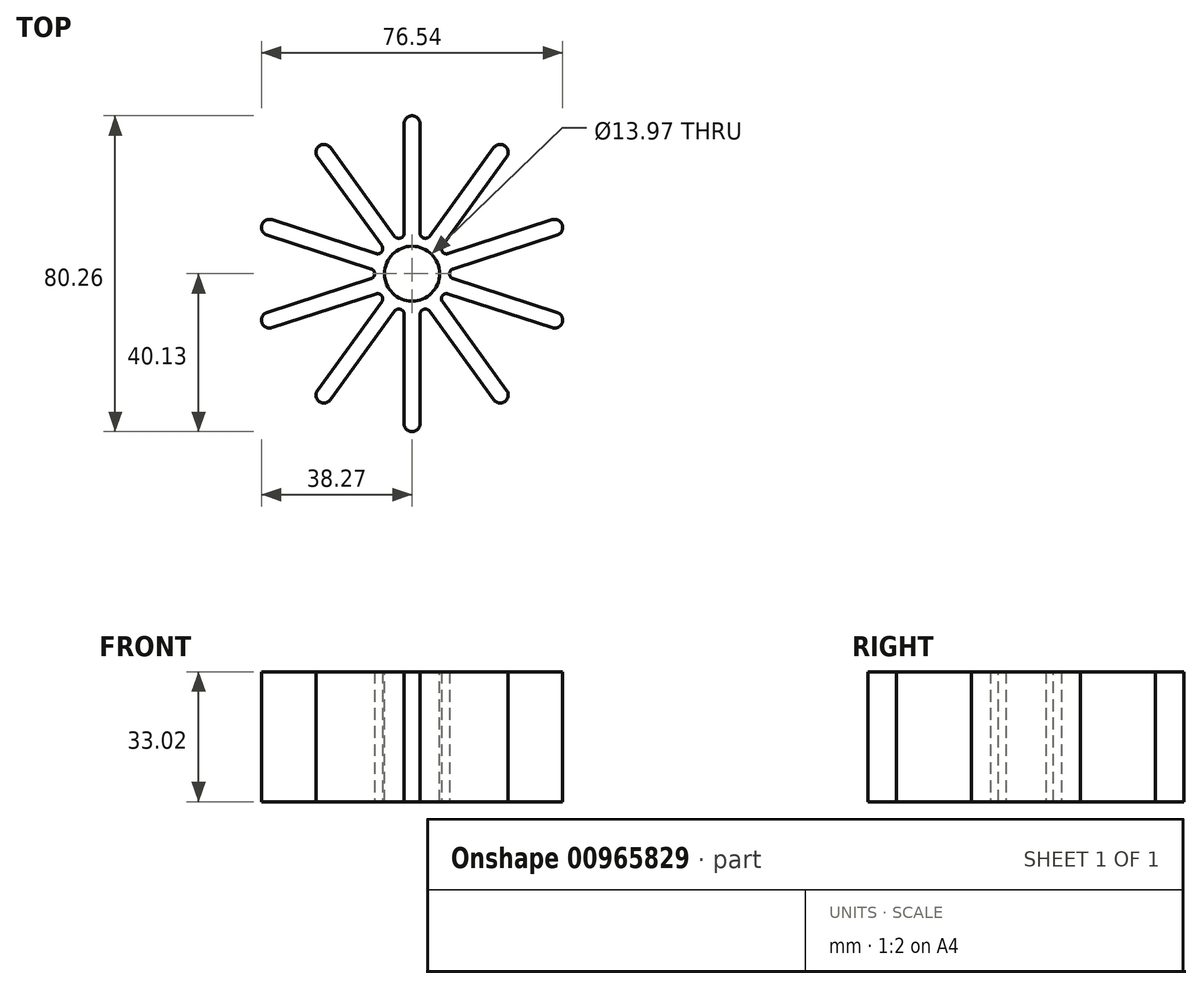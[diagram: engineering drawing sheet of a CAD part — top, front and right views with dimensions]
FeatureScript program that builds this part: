
annotation { "Feature Type Name" : "Feature", "Feature Type Description" : "" }
export const myFeature = defineFeature(function(context is Context, id is Id, definition is map)
    precondition{}
    {
        {
            var Q0;
            Q0=qCreatedBy(makeId("Top.planeOp"),FACE);
            var sketch = newSketch(context, id + "F0", { "sketchPlane" : qUnion([Q0])});
            skLineSegment(sketch, "E0", {"start": v(0, 0) * mm, "end": v(-2.03, 0) * mm});
            skLineSegment(sketch, "E1", {"start": v(-2.03, 0) * mm, "end": v(-2.03, 38.1) * mm});
            skArc(sketch, "E2", {"start": v(-2.03, 38.1) * mm, "mid": v(-1.44, 39.54) * mm, "end": v(0, 40.13) * mm});
            skLineSegment(sketch, "E3", {"start": v(0, 40.13) * mm, "end": v(0, 0) * mm});
            skArc(sketch, "E4.MirrorCS", {"start": v(2.03, 38.1) * mm, "mid": v(1.44, 39.54) * mm, "end": v(0, 40.13) * mm});
            skLineSegment(sketch, "E5.MirrorCS", {"start": v(2.03, 0) * mm, "end": v(2.03, 38.1) * mm});
            skLineSegment(sketch, "E6.MirrorCS", {"start": v(0, 0) * mm, "end": v(2.03, 0) * mm});
            skLineSegment(sketch, "E7.1.0", {"start": v(1.64, 1.2) * mm, "end": v(-20.75, 32.02) * mm});
            skLineSegment(sketch, "E7.1.1", {"start": v(-1.64, -1.2) * mm, "end": v(-24.04, 29.63) * mm});
            skLineSegment(sketch, "E7.1.2", {"start": v(-23.59, 32.47) * mm, "end": v(0, 0) * mm});
            skArc(sketch, "E7.1.3", {"start": v(-20.75, 32.02) * mm, "mid": v(-22.08, 32.83) * mm, "end": v(-23.59, 32.47) * mm});
            skArc(sketch, "E7.1.4", {"start": v(-24.04, 29.63) * mm, "mid": v(-24.4, 31.14) * mm, "end": v(-23.59, 32.47) * mm});
            skLineSegment(sketch, "E7.1.5", {"start": v(0, 0) * mm, "end": v(1.64, 1.2) * mm});
            skLineSegment(sketch, "E7.1.6", {"start": v(0, 0) * mm, "end": v(-1.64, -1.2) * mm});
            skLineSegment(sketch, "E7.2.0", {"start": v(0.63, 1.93) * mm, "end": v(-35.6, 13.7) * mm});
            skLineSegment(sketch, "E7.2.1", {"start": v(-0.63, -1.93) * mm, "end": v(-36.86, 9.84) * mm});
            skLineSegment(sketch, "E7.2.2", {"start": v(-38.17, 12.4) * mm, "end": v(0, 0) * mm});
            skArc(sketch, "E7.2.3", {"start": v(-35.6, 13.7) * mm, "mid": v(-37.16, 13.58) * mm, "end": v(-38.17, 12.4) * mm});
            skArc(sketch, "E7.2.4", {"start": v(-36.86, 9.84) * mm, "mid": v(-38.05, 10.85) * mm, "end": v(-38.17, 12.4) * mm});
            skLineSegment(sketch, "E7.2.5", {"start": v(0, 0) * mm, "end": v(0.63, 1.93) * mm});
            skLineSegment(sketch, "E7.2.6", {"start": v(0, 0) * mm, "end": v(-0.63, -1.93) * mm});
            skLineSegment(sketch, "E7.3.0", {"start": v(-0.63, 1.93) * mm, "end": v(-36.86, -9.84) * mm});
            skLineSegment(sketch, "E7.3.1", {"start": v(0.63, -1.93) * mm, "end": v(-35.6, -13.7) * mm});
            skLineSegment(sketch, "E7.3.2", {"start": v(-38.17, -12.4) * mm, "end": v(0, 0) * mm});
            skArc(sketch, "E7.3.3", {"start": v(-36.86, -9.84) * mm, "mid": v(-38.05, -10.85) * mm, "end": v(-38.17, -12.4) * mm});
            skArc(sketch, "E7.3.4", {"start": v(-35.6, -13.7) * mm, "mid": v(-37.16, -13.58) * mm, "end": v(-38.17, -12.4) * mm});
            skLineSegment(sketch, "E7.3.5", {"start": v(0, 0) * mm, "end": v(-0.63, 1.93) * mm});
            skLineSegment(sketch, "E7.3.6", {"start": v(0, 0) * mm, "end": v(0.63, -1.93) * mm});
            skLineSegment(sketch, "E7.4.0", {"start": v(-1.64, 1.2) * mm, "end": v(-24.04, -29.63) * mm});
            skLineSegment(sketch, "E7.4.1", {"start": v(1.64, -1.2) * mm, "end": v(-20.75, -32.02) * mm});
            skLineSegment(sketch, "E7.4.2", {"start": v(-23.59, -32.47) * mm, "end": v(0, 0) * mm});
            skArc(sketch, "E7.4.3", {"start": v(-24.04, -29.63) * mm, "mid": v(-24.4, -31.14) * mm, "end": v(-23.59, -32.47) * mm});
            skArc(sketch, "E7.4.4", {"start": v(-20.75, -32.02) * mm, "mid": v(-22.08, -32.83) * mm, "end": v(-23.59, -32.47) * mm});
            skLineSegment(sketch, "E7.4.5", {"start": v(0, 0) * mm, "end": v(-1.64, 1.2) * mm});
            skLineSegment(sketch, "E7.4.6", {"start": v(0, 0) * mm, "end": v(1.64, -1.2) * mm});
            skLineSegment(sketch, "E7.5.0", {"start": v(-2.03, 0) * mm, "end": v(-2.03, -38.1) * mm});
            skLineSegment(sketch, "E7.5.1", {"start": v(2.03, 0) * mm, "end": v(2.03, -38.1) * mm});
            skLineSegment(sketch, "E7.5.2", {"start": v(0, -40.13) * mm, "end": v(0, 0) * mm});
            skArc(sketch, "E7.5.3", {"start": v(-2.03, -38.1) * mm, "mid": v(-1.44, -39.54) * mm, "end": v(0, -40.13) * mm});
            skArc(sketch, "E7.5.4", {"start": v(2.03, -38.1) * mm, "mid": v(1.44, -39.54) * mm, "end": v(0, -40.13) * mm});
            skLineSegment(sketch, "E7.6.0", {"start": v(-1.64, -1.2) * mm, "end": v(20.75, -32.02) * mm});
            skLineSegment(sketch, "E7.6.1", {"start": v(1.64, 1.2) * mm, "end": v(24.04, -29.63) * mm});
            skLineSegment(sketch, "E7.6.2", {"start": v(23.59, -32.47) * mm, "end": v(0, 0) * mm});
            skArc(sketch, "E7.6.3", {"start": v(20.75, -32.02) * mm, "mid": v(22.08, -32.83) * mm, "end": v(23.59, -32.47) * mm});
            skArc(sketch, "E7.6.4", {"start": v(24.04, -29.63) * mm, "mid": v(24.4, -31.14) * mm, "end": v(23.59, -32.47) * mm});
            skLineSegment(sketch, "E7.6.5", {"start": v(0, 0) * mm, "end": v(-1.64, -1.2) * mm});
            skLineSegment(sketch, "E7.6.6", {"start": v(0, 0) * mm, "end": v(1.64, 1.2) * mm});
            skLineSegment(sketch, "E7.7.0", {"start": v(-0.63, -1.93) * mm, "end": v(35.6, -13.7) * mm});
            skLineSegment(sketch, "E7.7.1", {"start": v(0.63, 1.93) * mm, "end": v(36.86, -9.84) * mm});
            skLineSegment(sketch, "E7.7.2", {"start": v(38.17, -12.4) * mm, "end": v(0, 0) * mm});
            skArc(sketch, "E7.7.3", {"start": v(35.6, -13.7) * mm, "mid": v(37.16, -13.58) * mm, "end": v(38.17, -12.4) * mm});
            skArc(sketch, "E7.7.4", {"start": v(36.86, -9.84) * mm, "mid": v(38.05, -10.85) * mm, "end": v(38.17, -12.4) * mm});
            skLineSegment(sketch, "E7.7.5", {"start": v(0, 0) * mm, "end": v(-0.63, -1.93) * mm});
            skLineSegment(sketch, "E7.7.6", {"start": v(0, 0) * mm, "end": v(0.63, 1.93) * mm});
            skLineSegment(sketch, "E7.8.0", {"start": v(0.63, -1.93) * mm, "end": v(36.86, 9.84) * mm});
            skLineSegment(sketch, "E7.8.1", {"start": v(-0.63, 1.93) * mm, "end": v(35.6, 13.7) * mm});
            skLineSegment(sketch, "E7.8.2", {"start": v(38.17, 12.4) * mm, "end": v(0, 0) * mm});
            skArc(sketch, "E7.8.3", {"start": v(36.86, 9.84) * mm, "mid": v(38.05, 10.85) * mm, "end": v(38.17, 12.4) * mm});
            skArc(sketch, "E7.8.4", {"start": v(35.6, 13.7) * mm, "mid": v(37.16, 13.58) * mm, "end": v(38.17, 12.4) * mm});
            skLineSegment(sketch, "E7.8.5", {"start": v(0, 0) * mm, "end": v(0.63, -1.93) * mm});
            skLineSegment(sketch, "E7.8.6", {"start": v(0, 0) * mm, "end": v(-0.63, 1.93) * mm});
            skLineSegment(sketch, "E7.9.0", {"start": v(1.64, -1.2) * mm, "end": v(24.04, 29.63) * mm});
            skLineSegment(sketch, "E7.9.1", {"start": v(-1.64, 1.2) * mm, "end": v(20.75, 32.02) * mm});
            skLineSegment(sketch, "E7.9.2", {"start": v(23.59, 32.47) * mm, "end": v(0, 0) * mm});
            skArc(sketch, "E7.9.3", {"start": v(24.04, 29.63) * mm, "mid": v(24.4, 31.14) * mm, "end": v(23.59, 32.47) * mm});
            skArc(sketch, "E7.9.4", {"start": v(20.75, 32.02) * mm, "mid": v(22.08, 32.83) * mm, "end": v(23.59, 32.47) * mm});
            skLineSegment(sketch, "E7.9.5", {"start": v(0, 0) * mm, "end": v(1.64, -1.2) * mm});
            skLineSegment(sketch, "E7.9.6", {"start": v(0, 0) * mm, "end": v(-1.64, 1.2) * mm});
            skPoint(sketch, "E7.center", {"position": v(0, 0) * mm});
            skCircle(sketch, "E8", {"center": v(0, 0) * mm, "radius": 9.53 * mm});
            skSolve(sketch);
        }
        {
            var Q0;
            Q0 = qSketchRegion(id + "F0", true);
            extrude(context, id + "F1", {"entities" : qUnion([Q0]), "depth" : 33.02 * mm, "offsetDistance" : 25.4 * mm});
        }
        {
            var Q0;
            Q0=makeQuery(id+"F1.opExtrude","CAP_FACE",FACE,{"disambiguationData":[OSD([sQuery(id+"F0.wireOp",EDGE,"E1"),sQuery(id+"F0.wireOp",EDGE,"E2"),sQuery(id+"F0.wireOp",EDGE,"E4.MirrorCS"),sQuery(id+"F0.wireOp",EDGE,"E5.MirrorCS"),sQuery(id+"F0.wireOp",EDGE,"E7.1.0"),sQuery(id+"F0.wireOp",EDGE,"E7.1.1"),sQuery(id+"F0.wireOp",EDGE,"E7.1.3"),sQuery(id+"F0.wireOp",EDGE,"E7.1.4"),sQuery(id+"F0.wireOp",EDGE,"E7.2.0"),sQuery(id+"F0.wireOp",EDGE,"E7.2.1"),sQuery(id+"F0.wireOp",EDGE,"E7.2.3"),sQuery(id+"F0.wireOp",EDGE,"E7.2.4"),sQuery(id+"F0.wireOp",EDGE,"E7.3.0"),sQuery(id+"F0.wireOp",EDGE,"E7.3.1"),sQuery(id+"F0.wireOp",EDGE,"E7.3.3"),sQuery(id+"F0.wireOp",EDGE,"E7.3.4"),sQuery(id+"F0.wireOp",EDGE,"E7.4.0"),sQuery(id+"F0.wireOp",EDGE,"E7.4.1"),sQuery(id+"F0.wireOp",EDGE,"E7.4.3"),sQuery(id+"F0.wireOp",EDGE,"E7.4.4"),sQuery(id+"F0.wireOp",EDGE,"E7.5.0"),sQuery(id+"F0.wireOp",EDGE,"E7.5.1"),sQuery(id+"F0.wireOp",EDGE,"E7.5.3"),sQuery(id+"F0.wireOp",EDGE,"E7.5.4"),sQuery(id+"F0.wireOp",EDGE,"E7.6.0"),sQuery(id+"F0.wireOp",EDGE,"E7.6.1"),sQuery(id+"F0.wireOp",EDGE,"E7.6.3"),sQuery(id+"F0.wireOp",EDGE,"E7.6.4"),sQuery(id+"F0.wireOp",EDGE,"E7.7.0"),sQuery(id+"F0.wireOp",EDGE,"E7.7.1"),sQuery(id+"F0.wireOp",EDGE,"E7.7.3"),sQuery(id+"F0.wireOp",EDGE,"E7.7.4"),sQuery(id+"F0.wireOp",EDGE,"E7.8.0"),sQuery(id+"F0.wireOp",EDGE,"E7.8.1"),sQuery(id+"F0.wireOp",EDGE,"E7.8.3"),sQuery(id+"F0.wireOp",EDGE,"E7.8.4"),sQuery(id+"F0.wireOp",EDGE,"E7.9.0"),sQuery(id+"F0.wireOp",EDGE,"E7.9.1"),sQuery(id+"F0.wireOp",EDGE,"E7.9.3"),sQuery(id+"F0.wireOp",EDGE,"E7.9.4"),sQuery(id+"F0.wireOp",EDGE,"E8")])],"isStart":false});
            var sketch = newSketch(context, id + "F2", { "sketchPlane" : qUnion([Q0])});
            skCircle(sketch, "E9", {"center": v(0, 0) * mm, "radius": 6.99 * mm});
            skSolve(sketch);
        }
        {
            var Q0;
            Q0 = qSketchRegion(id + "F2", true);
            extrude(context, id + "F3", {"entities" : qUnion([Q0]), "operationType" : NewBodyOperationType.REMOVE, "endBound" : BoundingType.THROUGH_ALL, "oppositeDirection" : true, "depth" : 25.4 * mm, "offsetDistance" : 25.4 * mm});
        }
        {
            var Q0;
            Q0=makeQuery(id+"F1.opExtrude","SWEPT_EDGE",EDGE,{"disambiguationData":[OSD([sQuery(id+"F0.wireOp",EDGE,"E7.7.0"),sQuery(id+"F0.wireOp",EDGE,"E8")])]});
            var Q1;
            Q1=makeQuery(id+"F1.opExtrude","SWEPT_EDGE",EDGE,{"disambiguationData":[OSD([sQuery(id+"F0.wireOp",EDGE,"E7.6.1"),sQuery(id+"F0.wireOp",EDGE,"E8")])]});
            var Q2;
            Q2=makeQuery(id+"F1.opExtrude","SWEPT_EDGE",EDGE,{"disambiguationData":[OSD([sQuery(id+"F0.wireOp",EDGE,"E7.6.0"),sQuery(id+"F0.wireOp",EDGE,"E8")])]});
            var Q3;
            Q3=makeQuery(id+"F1.opExtrude","SWEPT_EDGE",EDGE,{"disambiguationData":[OSD([sQuery(id+"F0.wireOp",EDGE,"E7.5.1"),sQuery(id+"F0.wireOp",EDGE,"E8")])]});
            var Q4;
            Q4=makeQuery(id+"F1.opExtrude","SWEPT_EDGE",EDGE,{"disambiguationData":[OSD([sQuery(id+"F0.wireOp",EDGE,"E7.5.0"),sQuery(id+"F0.wireOp",EDGE,"E8")])]});
            var Q5;
            Q5=makeQuery(id+"F1.opExtrude","SWEPT_EDGE",EDGE,{"disambiguationData":[OSD([sQuery(id+"F0.wireOp",EDGE,"E7.4.1"),sQuery(id+"F0.wireOp",EDGE,"E8")])]});
            var Q6;
            Q6=makeQuery(id+"F1.opExtrude","SWEPT_EDGE",EDGE,{"disambiguationData":[OSD([sQuery(id+"F0.wireOp",EDGE,"E7.4.0"),sQuery(id+"F0.wireOp",EDGE,"E8")])]});
            var Q7;
            Q7=makeQuery(id+"F1.opExtrude","SWEPT_EDGE",EDGE,{"disambiguationData":[OSD([sQuery(id+"F0.wireOp",EDGE,"E7.3.1"),sQuery(id+"F0.wireOp",EDGE,"E8")])]});
            var Q8;
            Q8=makeQuery(id+"F1.opExtrude","SWEPT_EDGE",EDGE,{"disambiguationData":[OSD([sQuery(id+"F0.wireOp",EDGE,"E7.3.0"),sQuery(id+"F0.wireOp",EDGE,"E8")])]});
            var Q9;
            Q9=makeQuery(id+"F1.opExtrude","SWEPT_EDGE",EDGE,{"disambiguationData":[OSD([sQuery(id+"F0.wireOp",EDGE,"E7.2.1"),sQuery(id+"F0.wireOp",EDGE,"E8")])]});
            var Q10;
            Q10=makeQuery(id+"F1.opExtrude","SWEPT_EDGE",EDGE,{"disambiguationData":[OSD([sQuery(id+"F0.wireOp",EDGE,"E7.2.0"),sQuery(id+"F0.wireOp",EDGE,"E8")])]});
            var Q11;
            Q11=makeQuery(id+"F1.opExtrude","SWEPT_EDGE",EDGE,{"disambiguationData":[OSD([sQuery(id+"F0.wireOp",EDGE,"E7.1.1"),sQuery(id+"F0.wireOp",EDGE,"E8")])]});
            var Q12;
            Q12=makeQuery(id+"F1.opExtrude","SWEPT_EDGE",EDGE,{"disambiguationData":[OSD([sQuery(id+"F0.wireOp",EDGE,"E7.1.0"),sQuery(id+"F0.wireOp",EDGE,"E8")])]});
            var Q13;
            Q13=makeQuery(id+"F1.opExtrude","SWEPT_EDGE",EDGE,{"disambiguationData":[OSD([sQuery(id+"F0.wireOp",EDGE,"E1"),sQuery(id+"F0.wireOp",EDGE,"E8")])]});
            var Q14;
            Q14=makeQuery(id+"F1.opExtrude","SWEPT_EDGE",EDGE,{"disambiguationData":[OSD([sQuery(id+"F0.wireOp",EDGE,"E5.MirrorCS"),sQuery(id+"F0.wireOp",EDGE,"E8")])]});
            var Q15;
            Q15=makeQuery(id+"F1.opExtrude","SWEPT_EDGE",EDGE,{"disambiguationData":[OSD([sQuery(id+"F0.wireOp",EDGE,"E7.9.1"),sQuery(id+"F0.wireOp",EDGE,"E8")])]});
            var Q16;
            Q16=makeQuery(id+"F1.opExtrude","SWEPT_EDGE",EDGE,{"disambiguationData":[OSD([sQuery(id+"F0.wireOp",EDGE,"E7.8.1"),sQuery(id+"F0.wireOp",EDGE,"E8")])]});
            var Q17;
            Q17=makeQuery(id+"F1.opExtrude","SWEPT_EDGE",EDGE,{"disambiguationData":[OSD([sQuery(id+"F0.wireOp",EDGE,"E7.9.0"),sQuery(id+"F0.wireOp",EDGE,"E8")])]});
            var Q18;
            Q18=makeQuery(id+"F1.opExtrude","SWEPT_EDGE",EDGE,{"disambiguationData":[OSD([sQuery(id+"F0.wireOp",EDGE,"E7.7.1"),sQuery(id+"F0.wireOp",EDGE,"E8")])]});
            var Q19;
            Q19=makeQuery(id+"F1.opExtrude","SWEPT_EDGE",EDGE,{"disambiguationData":[OSD([sQuery(id+"F0.wireOp",EDGE,"E7.8.0"),sQuery(id+"F0.wireOp",EDGE,"E8")])]});
            fillet(context, id + "F4", {"entities" : qUnion([Q0, Q1, Q2, Q3, Q4, Q5, Q6, Q7, Q8, Q9, Q10, Q11, Q12, Q13, Q14, Q15, Q16, Q17, Q18, Q19]), "radius" : 1.27 * mm, "tangentPropagation" : true, "allowEdgeOverflow" : false});
        }
    });
